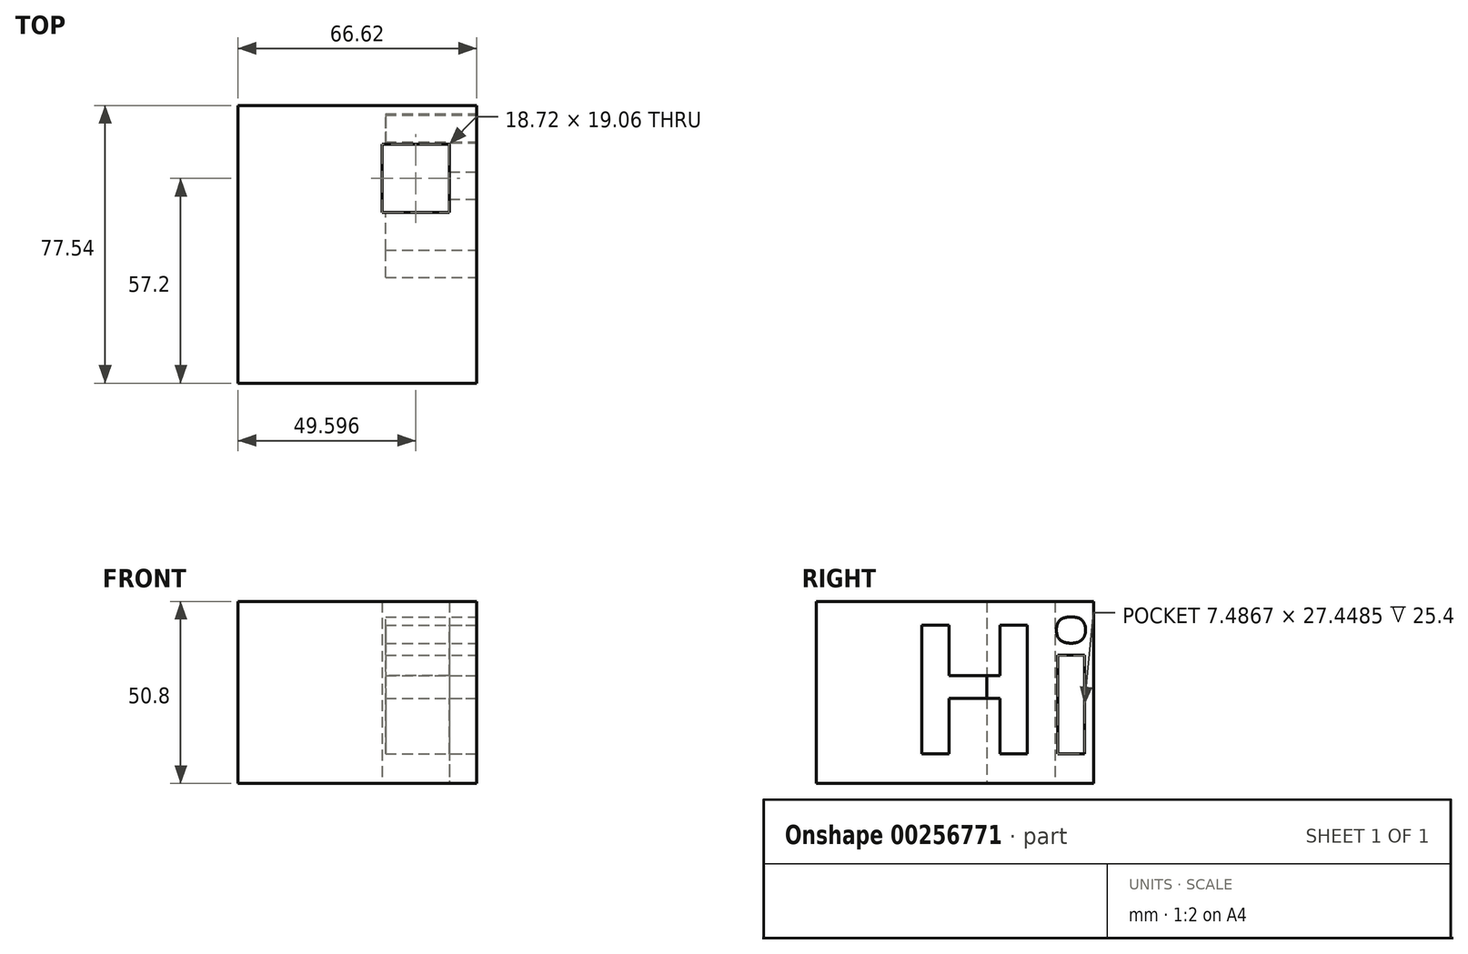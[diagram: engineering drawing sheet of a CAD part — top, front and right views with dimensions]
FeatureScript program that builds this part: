
annotation { "Feature Type Name" : "Feature", "Feature Type Description" : "" }
export const myFeature = defineFeature(function(context is Context, id is Id, definition is map)
    precondition{}
    {
        {
            var Q0;
            Q0=qCreatedBy(makeId("Top.planeOp"),FACE);
            var sketch = newSketch(context, id + "F0", { "sketchPlane" : qUnion([Q0])});
            skLineSegment(sketch, "E0.bottom", {"start": v(-33.31, 38.77) * mm, "end": v(33.31, 38.77) * mm});
            skLineSegment(sketch, "E0.top", {"start": v(-33.31, -38.77) * mm, "end": v(33.31, -38.77) * mm});
            skLineSegment(sketch, "E0.left", {"start": v(-33.31, 38.77) * mm, "end": v(-33.31, -38.77) * mm});
            skLineSegment(sketch, "E0.right", {"start": v(33.31, 38.77) * mm, "end": v(33.31, -38.77) * mm});
            skPoint(sketch, "E0.middle", {"position": v(0, 0) * mm});
            skSolve(sketch);
        }
        {
            var Q0;
            Q0 = qSketchRegion(id + "F0", true);
            extrude(context, id + "F1", {"entities" : qUnion([Q0]), "depth" : 50.8 * mm});
        }
        {
            var Q0;
            Q0=qCreatedBy(makeId("Top.planeOp"),FACE);
            var sketch = newSketch(context, id + "F2", { "sketchPlane" : qUnion([Q0])});
            skLineSegment(sketch, "E1.bottom", {"start": v(6.93, 27.96) * mm, "end": v(25.65, 27.96) * mm});
            skLineSegment(sketch, "E1.top", {"start": v(6.93, 8.9) * mm, "end": v(25.65, 8.9) * mm});
            skLineSegment(sketch, "E1.left", {"start": v(6.93, 27.96) * mm, "end": v(6.93, 8.9) * mm});
            skLineSegment(sketch, "E1.right", {"start": v(25.65, 27.96) * mm, "end": v(25.65, 8.9) * mm});
            skSolve(sketch);
        }
        {
            var Q0;
            Q0 = qSketchRegion(id + "F2", true);
            extrude(context, id + "F3", {"entities" : qUnion([Q0]), "operationType" : NewBodyOperationType.REMOVE, "endBound" : BoundingType.UP_TO_NEXT, "depth" : 3 * mm});
        }
        {
            var Q0;
            Q0=makeQuery(id+"F1.opExtrude","SWEPT_FACE",FACE,{"disambiguationData":[OSD([sQuery(id+"F0.wireOp",EDGE,"E0.right")])]});
            var sketch = newSketch(context, id + "F4", { "sketchPlane" : qUnion([Q0])});
            skText(sketch, "E2", { "text": "Hi", "fontName": "OpenSans-Bold.ttf"});
            const initialGuessF4  = {"E2": [-0.01373, 0.0083, 1, 0, 0.0362]};
            skSetInitialGuess(sketch, initialGuessF4);
            skSolve(sketch);
        }
        {
            var Q0;
            Q0 = qSketchRegion(id + "F4", true);
            extrude(context, id + "F5", {"entities" : qUnion([Q0]), "operationType" : NewBodyOperationType.REMOVE, "oppositeDirection" : true, "depth" : 25.4 * mm});
        }
    });
